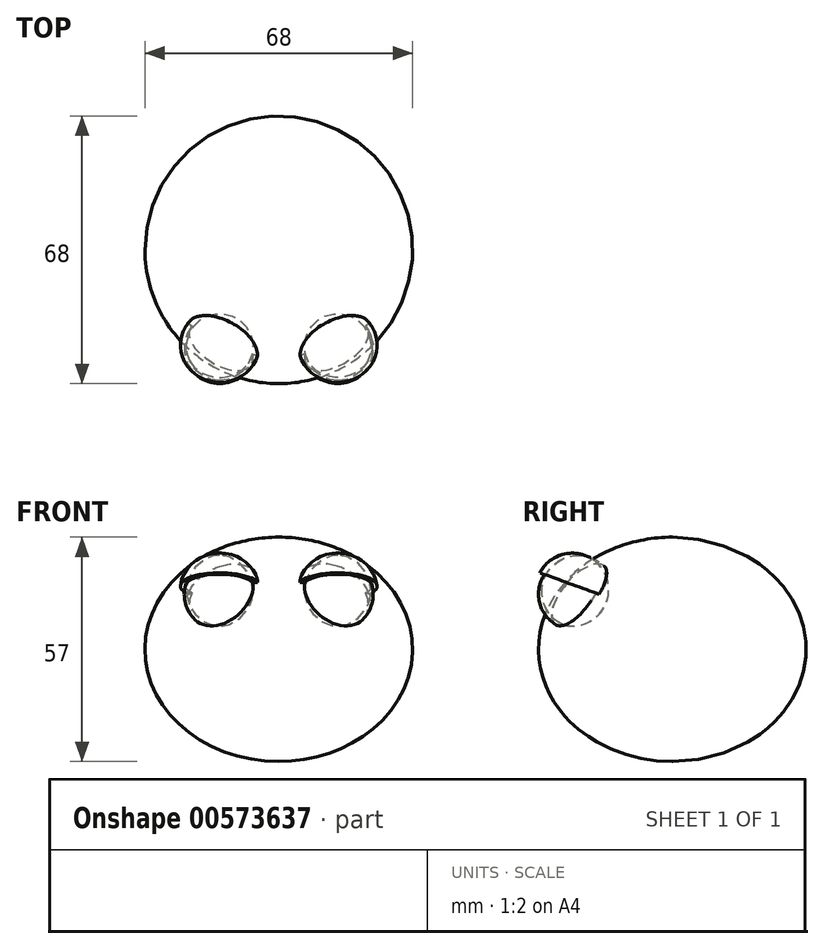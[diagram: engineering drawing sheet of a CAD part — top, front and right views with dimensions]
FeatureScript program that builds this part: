
annotation { "Feature Type Name" : "Feature", "Feature Type Description" : "" }
export const myFeature = defineFeature(function(context is Context, id is Id, definition is map)
    precondition{}
    {
        {
            var Q0;
            Q0=qCreatedBy(makeId("Front.planeOp"),FACE);
            var sketch = newSketch(context, id + "F0", { "sketchPlane" : qUnion([Q0])});
            skEllipticalArc(sketch, "E0", {});
            skLineSegment(sketch, "E1", {"start": v(0, 0) * mm, "end": v(0, 39.84) * mm, "construction": true});
            skLineSegment(sketch, "E2", {"start": v(0, 28.5) * mm, "end": v(0, -28.5) * mm});
            const initialGuessF0  = {"E0": [0, 0, -1, 0, 0.034, 0.0285, 4.71238898038469, 1.5707963267948966]};
            skSetInitialGuess(sketch, initialGuessF0);
            skSolve(sketch);
        }
        {
            var Q0;
            Q0=makeQuery(id+"F0.imprint","IMPRINT",FACE,{"disambiguationData":[TD([[makeQuery(id+"F0.imprint","IMPRINT",EDGE,{"derivedFrom":sQuery(id+"F0.wireOp",EDGE,"E0")}),1.0]])]});
            var Q1;
            Q1=sQuery(id+"F0.wireOp",EDGE,"E1");
            revolve(context, id + "F1", {"entities" : qUnion([Q0]), "axis" : qUnion([Q1]), "revolveType" : RevolveType.FULL});
        }
        {
            var Q0;
            Q0=qCreatedBy(makeId("Front.planeOp"),FACE);
            cPlane(context, id + "F2", {"entities" : qUnion([Q0]), "cplaneType" : CPlaneType.OFFSET, "offset" : 25 * mm, "width" : 150 * mm, "height" : 150 * mm});
        }
        {
            var Q0;
            Q0=qCreatedBy(id+"F2.planeOp",FACE);
            var sketch = newSketch(context, id + "F3", { "sketchPlane" : qUnion([Q0])});
            skArc(sketch, "E3", {"start": v(-15, 23) * mm, "mid": v(-24, 14) * mm, "end": v(-15, 5) * mm});
            skArc(sketch, "E4", {"start": v(15, 23) * mm, "mid": v(6, 14) * mm, "end": v(15, 5) * mm});
            skLineSegment(sketch, "E5", {"start": v(-15, 14) * mm, "end": v(0, 14) * mm, "construction": true});
            skLineSegment(sketch, "E6", {"start": v(0, 14) * mm, "end": v(15, 14) * mm, "construction": true});
            skLineSegment(sketch, "E7", {"start": v(0, 14) * mm, "end": v(0, 0) * mm, "construction": true});
            skLineSegment(sketch, "E8", {"start": v(-15, 14) * mm, "end": v(-15, 30.53) * mm, "construction": true});
            skLineSegment(sketch, "E9", {"start": v(15, 14) * mm, "end": v(15, 30.53) * mm, "construction": true});
            skLineSegment(sketch, "E10", {"start": v(-15, 23) * mm, "end": v(-15, 5) * mm});
            skLineSegment(sketch, "E11", {"start": v(15, 23) * mm, "end": v(15, 5) * mm});
            skSolve(sketch);
        }
        {
            var Q0;
            Q0=makeQuery(id+"F3.imprint","IMPRINT",FACE,{"disambiguationData":[TD([[makeQuery(id+"F3.imprint","IMPRINT",EDGE,{"derivedFrom":sQuery(id+"F3.wireOp",EDGE,"E3")}),1.0]])]});
            var Q1;
            Q1=sQuery(id+"F3.wireOp",EDGE,"E8");
            revolve(context, id + "F4", {"operationType" : NewBodyOperationType.ADD, "entities" : qUnion([Q0]), "axis" : qUnion([Q1]), "revolveType" : RevolveType.FULL});
        }
        {
            var Q0;
            Q0=makeQuery(id+"F3.imprint","IMPRINT",FACE,{"disambiguationData":[TD([[makeQuery(id+"F3.imprint","IMPRINT",EDGE,{"derivedFrom":sQuery(id+"F3.wireOp",EDGE,"E4")}),1.0]])]});
            var Q1;
            Q1=sQuery(id+"F3.wireOp",EDGE,"E9");
            revolve(context, id + "F5", {"operationType" : NewBodyOperationType.ADD, "entities" : qUnion([Q0]), "axis" : qUnion([Q1]), "revolveType" : RevolveType.FULL});
        }
        {
            var Q0;
            Q0=qCreatedBy(id+"F2.planeOp",FACE);
            var Q1;
            Q1=sQuery(id+"F3.wireOp",EDGE,"E5");
            cPlane(context, id + "F6", {"entities" : qUnion([Q0, Q1]), "cplaneType" : CPlaneType.LINE_ANGLE, "offset" : 25 * mm, "angle" : 160 * degree, "width" : 150 * mm, "height" : 150 * mm});
        }
        {
            var Q0;
            Q0=qCreatedBy(id+"F6.planeOp",FACE);
            var sketch = newSketch(context, id + "F7", { "sketchPlane" : qUnion([Q0])});
            skArc(sketch, "E12", {"start": v(-5, 6.78) * mm, "mid": v(-8.4, 12.78) * mm, "end": v(-15, 14.78) * mm});
            skLineSegment(sketch, "E13", {"start": v(-15, 4.78) * mm, "end": v(-15, 14.78) * mm});
            skLineSegment(sketch, "E14", {"start": v(-15, 4.78) * mm, "end": v(-15, 21.63) * mm, "construction": true});
            skArc(sketch, "E15", {"start": v(-5, 6.78) * mm, "mid": v(-10.14, 6.49) * mm, "end": v(-15, 4.78) * mm});
            skSolve(sketch);
        }
        {
            var Q0;
            Q0 = qSketchRegion(id + "F7", true);
            var Q1;
            Q1 = qConstructionFilter(qBodyType(qCreatedBy(id + "F7" ,EDGE), BodyType.WIRE), ConstructionObject.NO);
            var Q2;
            Q2=sQuery(id+"F7.wireOp",EDGE,"E14");
            revolve(context, id + "F8", {"operationType" : NewBodyOperationType.ADD, "entities" : qUnion([Q0]), "surfaceEntities" : qUnion([Q1]), "axis" : qUnion([Q2]), "revolveType" : RevolveType.FULL});
        }
        {
            var Q0;
            Q0=makeQuery(id+"F1.opRevolve","SWEPT_BODY",BODY,{"disambiguationData":[OSD([sQuery(id+"F0.wireOp",EDGE,"E0"),sQuery(id+"F0.wireOp",EDGE,"E2")])]});
            var Q1;
            Q1=qCreatedBy(makeId("Right.planeOp"),FACE);
            mirror(context, id + "F9", {"operationType" : NewBodyOperationType.ADD, "entities" : qUnion([Q0]), "mirrorPlane" : qUnion([Q1])});
        }
    });
